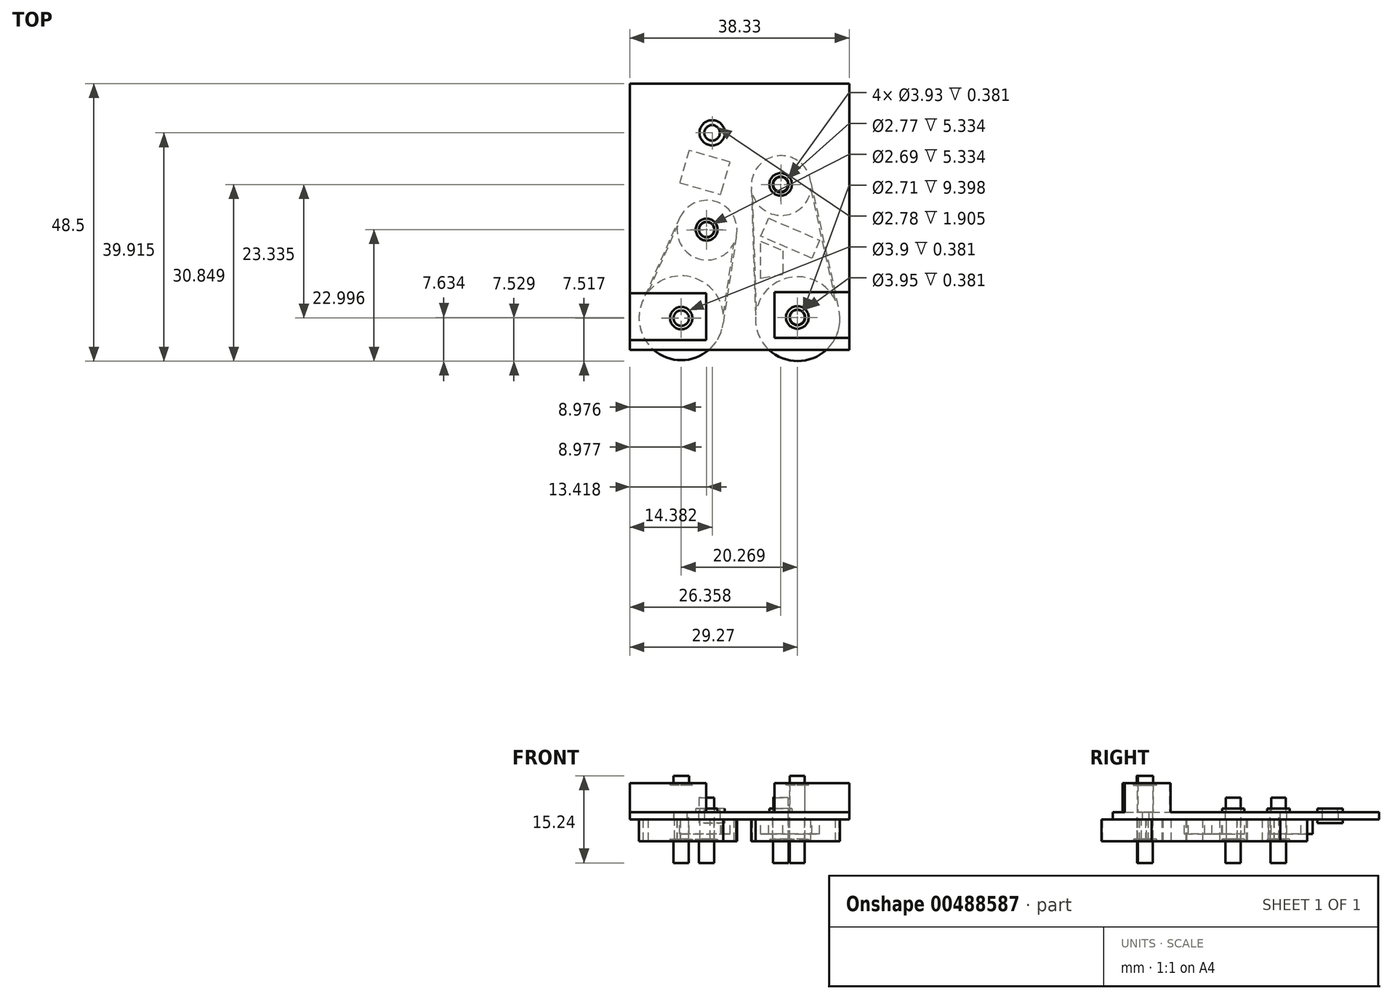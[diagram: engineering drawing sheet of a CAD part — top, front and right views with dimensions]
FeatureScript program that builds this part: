
annotation { "Feature Type Name" : "Feature", "Feature Type Description" : "" }
export const myFeature = defineFeature(function(context is Context, id is Id, definition is map)
    precondition{}
    {
        {
            var Q0;
            Q0=qCreatedBy(makeId("Top.planeOp"),FACE);
            var sketch = newSketch(context, id + "F0", { "sketchPlane" : qUnion([Q0])});
            skLineSegment(sketch, "E0", {"start": v(0, 0) * mm, "end": v(38.33, 0) * mm});
            skLineSegment(sketch, "E1", {"start": v(38.33, 0) * mm, "end": v(38.33, -46.53) * mm});
            skLineSegment(sketch, "E2", {"start": v(38.33, -46.53) * mm, "end": v(0, -46.53) * mm});
            skLineSegment(sketch, "E3", {"start": v(0, -46.53) * mm, "end": v(0, 0) * mm});
            skSolve(sketch);
        }
        {
            var Q0;
            Q0 = qSketchRegion(id + "F0", true);
            extrude(context, id + "F1", {"entities" : qUnion([Q0]), "depth" : 1.27 * mm});
        }
        {
            var Q0;
            Q0=makeQuery(id+"F1.opExtrude","CAP_FACE",FACE,{"disambiguationData":[OSD([sQuery(id+"F0.wireOp",EDGE,"E0"),sQuery(id+"F0.wireOp",EDGE,"E1"),sQuery(id+"F0.wireOp",EDGE,"E2"),sQuery(id+"F0.wireOp",EDGE,"E3")])],"isStart":true});
            var sketch = newSketch(context, id + "F2", { "sketchPlane" : qUnion([Q0])});
            skCircle(sketch, "E4", {"center": v(8.98, 40.97) * mm, "radius": 7.37 * mm});
            skCircle(sketch, "E5", {"center": v(29.32, 41.13) * mm, "radius": 7.37 * mm});
            skSolve(sketch);
        }
        {
            var Q0;
            Q0 = qSketchRegion(id + "F2", true);
            extrude(context, id + "F3", {"entities" : qUnion([Q0]), "operationType" : NewBodyOperationType.ADD, "depth" : 3.8 * mm});
        }
        {
            var Q0;
            Q0=makeQuery(id+"F1.opExtrude","CAP_FACE",FACE,{"disambiguationData":[OSD([sQuery(id+"F0.wireOp",EDGE,"E0"),sQuery(id+"F0.wireOp",EDGE,"E1"),sQuery(id+"F0.wireOp",EDGE,"E2"),sQuery(id+"F0.wireOp",EDGE,"E3")])],"isStart":true});
            var sketch = newSketch(context, id + "F4", { "sketchPlane" : qUnion([Q0])});
            skCircle(sketch, "E6", {"center": v(13.5, 25.6) * mm, "radius": 5.22 * mm});
            skCircle(sketch, "E7", {"center": v(26.44, 17.81) * mm, "radius": 5.22 * mm});
            skSolve(sketch);
        }
        {
            var Q0;
            Q0 = qSketchRegion(id + "F4", true);
            extrude(context, id + "F5", {"entities" : qUnion([Q0]), "operationType" : NewBodyOperationType.ADD, "depth" : 3.8 * mm});
        }
        {
            var Q0;
            Q0=makeQuery(id+"F1.opExtrude","CAP_FACE",FACE,{"disambiguationData":[OSD([sQuery(id+"F0.wireOp",EDGE,"E0"),sQuery(id+"F0.wireOp",EDGE,"E1"),sQuery(id+"F0.wireOp",EDGE,"E2"),sQuery(id+"F0.wireOp",EDGE,"E3")])],"isStart":true});
            var sketch = newSketch(context, id + "F6", { "sketchPlane" : qUnion([Q0])});
            skCircle(sketch, "E8", {"center": v(14.38, 8.59) * mm, "radius": 1.36 * mm});
            skSolve(sketch);
        }
        {
            var Q0;
            Q0 = qSketchRegion(id + "F6", true);
            extrude(context, id + "F7", {"entities" : qUnion([Q0]), "operationType" : NewBodyOperationType.REMOVE, "oppositeDirection" : true, "depth" : 25.4 * mm});
        }
        {
            var Q0;
            Q0=makeQuery(id+"F1.opExtrude","CAP_FACE",FACE,{"disambiguationData":[OSD([sQuery(id+"F0.wireOp",EDGE,"E0"),sQuery(id+"F0.wireOp",EDGE,"E1"),sQuery(id+"F0.wireOp",EDGE,"E2"),sQuery(id+"F0.wireOp",EDGE,"E3")])],"isStart":true});
            var sketch = newSketch(context, id + "F8", { "sketchPlane" : qUnion([Q0])});
            skCircle(sketch, "E9", {"center": v(14.38, 8.59) * mm, "radius": 2.25 * mm});
            skSolve(sketch);
        }
        {
            var Q0;
            Q0 = qSketchRegion(id + "F8", true);
            extrude(context, id + "F9", {"entities" : qUnion([Q0]), "operationType" : NewBodyOperationType.ADD, "depth" : 0.64 * mm});
        }
        {
            var Q0;
            Q0=makeQuery(id+"F9.opExtrude","CAP_FACE",FACE,{"disambiguationData":[OSD([sQuery(id+"F8.wireOp",EDGE,"E9")])],"isStart":false});
            var sketch = newSketch(context, id + "F10", { "sketchPlane" : qUnion([Q0])});
            skCircle(sketch, "E10", {"center": v(14.38, 8.59) * mm, "radius": 1.39 * mm});
            skSolve(sketch);
        }
        {
            var Q0;
            Q0 = qSketchRegion(id + "F10", true);
            extrude(context, id + "F11", {"entities" : qUnion([Q0]), "operationType" : NewBodyOperationType.REMOVE, "oppositeDirection" : true, "depth" : 25.4 * mm});
        }
        {
            var Q0;
            Q0=makeQuery(id+"F1.opExtrude","CAP_FACE",FACE,{"disambiguationData":[OSD([sQuery(id+"F0.wireOp",EDGE,"E0"),sQuery(id+"F0.wireOp",EDGE,"E1"),sQuery(id+"F0.wireOp",EDGE,"E2"),sQuery(id+"F0.wireOp",EDGE,"E3")])],"isStart":true});
            var sketch = newSketch(context, id + "F12", { "sketchPlane" : qUnion([Q0])});
            skLineSegment(sketch, "E11", {"start": v(24.24, 23.52) * mm, "end": v(33.15, 27.36) * mm});
            skLineSegment(sketch, "E12", {"start": v(33.15, 27.36) * mm, "end": v(31.8, 30.5) * mm});
            skLineSegment(sketch, "E13", {"start": v(31.8, 30.5) * mm, "end": v(22.88, 26.67) * mm});
            skLineSegment(sketch, "E14", {"start": v(22.88, 26.67) * mm, "end": v(24.24, 23.52) * mm});
            skLineSegment(sketch, "E15", {"start": v(22.88, 34.06) * mm, "end": v(22.88, 27.52) * mm});
            skLineSegment(sketch, "E16", {"start": v(22.88, 27.52) * mm, "end": v(26.75, 29.2) * mm});
            skLineSegment(sketch, "E17", {"start": v(26.75, 29.2) * mm, "end": v(26.75, 33.38) * mm});
            skLineSegment(sketch, "E18", {"start": v(26.75, 33.38) * mm, "end": v(22.88, 34.06) * mm});
            skLineSegment(sketch, "E19", {"start": v(16.03, 18.85) * mm, "end": v(17.5, 13.68) * mm});
            skLineSegment(sketch, "E20", {"start": v(17.5, 13.68) * mm, "end": v(10.33, 11.65) * mm});
            skLineSegment(sketch, "E21", {"start": v(10.33, 11.65) * mm, "end": v(8.72, 17.32) * mm});
            skLineSegment(sketch, "E22", {"start": v(8.72, 17.32) * mm, "end": v(15.86, 19.35) * mm});
            skLineSegment(sketch, "E23", {"start": v(15.86, 19.35) * mm, "end": v(16.03, 18.85) * mm});
            skSolve(sketch);
        }
        {
            var Q0;
            Q0 = qSketchRegion(id + "F12", true);
            extrude(context, id + "F13", {"entities" : qUnion([Q0]), "operationType" : NewBodyOperationType.ADD, "depth" : 2.54 * mm});
        }
        {
            var Q0;
            Q0=makeQuery(id+"F3.opExtrude","CAP_FACE",FACE,{"disambiguationData":[OSD([sQuery(id+"F2.wireOp",EDGE,"E4")])],"isStart":false});
            var sketch = newSketch(context, id + "F14", { "sketchPlane" : qUnion([Q0])});
            skCircle(sketch, "E24", {"center": v(8.98, 40.97) * mm, "radius": 1.32 * mm});
            skCircle(sketch, "E25", {"center": v(29.26, 40.85) * mm, "radius": 1.32 * mm});
            skCircle(sketch, "E26", {"center": v(13.42, 25.5) * mm, "radius": 1.32 * mm});
            skCircle(sketch, "E27", {"center": v(26.35, 17.6) * mm, "radius": 1.38 * mm});
            skSolve(sketch);
        }
        {
            var Q0;
            Q0 = qSketchRegion(id + "F14", true);
            extrude(context, id + "F15", {"entities" : qUnion([Q0]), "operationType" : NewBodyOperationType.REMOVE, "oppositeDirection" : true, "depth" : 25.4 * mm});
        }
        {
            var Q0;
            Q0=makeQuery(id+"F3.opExtrude","CAP_FACE",FACE,{"disambiguationData":[OSD([sQuery(id+"F2.wireOp",EDGE,"E4")])],"isStart":false});
            var sketch = newSketch(context, id + "F16", { "sketchPlane" : qUnion([Q0])});
            skCircle(sketch, "E28", {"center": v(8.98, 40.97) * mm, "radius": 1.96 * mm});
            skCircle(sketch, "E29", {"center": v(29.25, 40.9) * mm, "radius": 1.96 * mm});
            skCircle(sketch, "E30", {"center": v(13.37, 25.56) * mm, "radius": 1.96 * mm});
            skCircle(sketch, "E31", {"center": v(26.38, 17.64) * mm, "radius": 1.96 * mm});
            skSolve(sketch);
        }
        {
            var Q0;
            Q0 = qSketchRegion(id + "F16", true);
            extrude(context, id + "F17", {"entities" : qUnion([Q0]), "operationType" : NewBodyOperationType.REMOVE, "oppositeDirection" : true, "depth" : 0.38 * mm});
        }
        {
            var Q0;
            Q0=makeQuery(id+"F1.opExtrude","CAP_FACE",FACE,{"disambiguationData":[OSD([sQuery(id+"F0.wireOp",EDGE,"E0"),sQuery(id+"F0.wireOp",EDGE,"E1"),sQuery(id+"F0.wireOp",EDGE,"E2"),sQuery(id+"F0.wireOp",EDGE,"E3")])],"isStart":false});
            var sketch = newSketch(context, id + "F18", { "sketchPlane" : qUnion([Q0])});
            skLineSegment(sketch, "E32.bottom", {"start": v(13.33, -44.85) * mm, "end": v(0, -44.85) * mm});
            skLineSegment(sketch, "E32.top", {"start": v(13.33, -36.63) * mm, "end": v(0, -36.63) * mm});
            skLineSegment(sketch, "E32.left", {"start": v(13.33, -44.85) * mm, "end": v(13.33, -36.63) * mm});
            skLineSegment(sketch, "E32.right", {"start": v(0, -44.85) * mm, "end": v(0, -36.63) * mm});
            skLineSegment(sketch, "E33.bottom", {"start": v(25.27, -44.47) * mm, "end": v(38.33, -44.47) * mm});
            skLineSegment(sketch, "E33.top", {"start": v(25.27, -36.43) * mm, "end": v(38.33, -36.43) * mm});
            skLineSegment(sketch, "E33.left", {"start": v(25.27, -44.47) * mm, "end": v(25.27, -36.43) * mm});
            skLineSegment(sketch, "E33.right", {"start": v(38.33, -44.47) * mm, "end": v(38.33, -36.43) * mm});
            skSolve(sketch);
        }
        {
            var Q0;
            Q0 = qSketchRegion(id + "F18", true);
            extrude(context, id + "F19", {"entities" : qUnion([Q0]), "operationType" : NewBodyOperationType.ADD, "depth" : 5.08 * mm});
        }
        {
            var Q0;
            Q0=makeQuery(id+"F19.opExtrude","CAP_FACE",FACE,{"disambiguationData":[OSD([sQuery(id+"F18.wireOp",EDGE,"E33.bottom"),sQuery(id+"F18.wireOp",EDGE,"E33.top"),sQuery(id+"F18.wireOp",EDGE,"E33.left"),sQuery(id+"F18.wireOp",EDGE,"E33.right")])],"isStart":false});
            var sketch = newSketch(context, id + "F20", { "sketchPlane" : qUnion([Q0])});
            skCircle(sketch, "E34", {"center": v(29.27, -40.87) * mm, "radius": 1.35 * mm});
            skCircle(sketch, "E35", {"center": v(8.98, -40.98) * mm, "radius": 1.32 * mm});
            skSolve(sketch);
        }
        {
            var Q0;
            Q0 = qSketchRegion(id + "F20", true);
            extrude(context, id + "F21", {"entities" : qUnion([Q0]), "operationType" : NewBodyOperationType.REMOVE, "oppositeDirection" : true, "depth" : 25.4 * mm});
        }
        {
            var Q0;
            Q0=makeQuery(id+"F19.opExtrude","CAP_FACE",FACE,{"disambiguationData":[OSD([sQuery(id+"F18.wireOp",EDGE,"E33.bottom"),sQuery(id+"F18.wireOp",EDGE,"E33.top"),sQuery(id+"F18.wireOp",EDGE,"E33.left"),sQuery(id+"F18.wireOp",EDGE,"E33.right")])],"isStart":false});
            var sketch = newSketch(context, id + "F22", { "sketchPlane" : qUnion([Q0])});
            skCircle(sketch, "E36", {"center": v(29.27, -40.87) * mm, "radius": 1.98 * mm});
            skCircle(sketch, "E37", {"center": v(8.98, -40.98) * mm, "radius": 1.95 * mm});
            skSolve(sketch);
        }
        {
            var Q0;
            Q0 = qSketchRegion(id + "F22", true);
            extrude(context, id + "F23", {"entities" : qUnion([Q0]), "operationType" : NewBodyOperationType.REMOVE, "oppositeDirection" : true, "depth" : 0.38 * mm});
        }
        {
            var Q0;
            Q0=makeQuery(id+"F1.opExtrude","CAP_FACE",FACE,{"disambiguationData":[OSD([sQuery(id+"F0.wireOp",EDGE,"E0"),sQuery(id+"F0.wireOp",EDGE,"E1"),sQuery(id+"F0.wireOp",EDGE,"E2"),sQuery(id+"F0.wireOp",EDGE,"E3")])],"isStart":false});
            var sketch = newSketch(context, id + "F24", { "sketchPlane" : qUnion([Q0])});
            skCircle(sketch, "E38", {"center": v(13.42, -25.5) * mm, "radius": 1.91 * mm});
            skCircle(sketch, "E39", {"center": v(26.35, -17.6) * mm, "radius": 1.97 * mm});
            skCircle(sketch, "E40", {"center": v(14.38, -8.59) * mm, "radius": 2.2 * mm});
            skSolve(sketch);
        }
        {
            var Q0;
            Q0 = qSketchRegion(id + "F24", true);
            extrude(context, id + "F25", {"entities" : qUnion([Q0]), "operationType" : NewBodyOperationType.ADD, "depth" : 0.64 * mm});
        }
        {
            var Q0;
            Q0=makeQuery(id+"F25.opExtrude","CAP_FACE",FACE,{"disambiguationData":[OSD([sQuery(id+"F24.wireOp",EDGE,"E38")])],"isStart":false});
            var sketch = newSketch(context, id + "F26", { "sketchPlane" : qUnion([Q0])});
            skCircle(sketch, "E41", {"center": v(13.42, -25.5) * mm, "radius": 1.35 * mm});
            skCircle(sketch, "E42", {"center": v(26.36, -17.65) * mm, "radius": 1.38 * mm});
            skCircle(sketch, "E43", {"center": v(14.37, -8.6) * mm, "radius": 1.35 * mm});
            skSolve(sketch);
        }
        {
            var Q0;
            Q0 = qSketchRegion(id + "F26", true);
            extrude(context, id + "F27", {"entities" : qUnion([Q0]), "operationType" : NewBodyOperationType.REMOVE, "oppositeDirection" : true, "depth" : 25.4 * mm});
        }
        {
            var Q0;
            Q0=makeQuery(id+"F1.opExtrude","CAP_FACE",FACE,{"disambiguationData":[OSD([sQuery(id+"F0.wireOp",EDGE,"E0"),sQuery(id+"F0.wireOp",EDGE,"E1"),sQuery(id+"F0.wireOp",EDGE,"E2"),sQuery(id+"F0.wireOp",EDGE,"E3")])],"isStart":false});
            var sketch = newSketch(context, id + "F28", { "sketchPlane" : qUnion([Q0])});
            skCircle(sketch, "E44", {"center": v(29.26, -40.85) * mm, "radius": 1.3 * mm});
            skCircle(sketch, "E45", {"center": v(8.97, -41) * mm, "radius": 1.35 * mm});
            skSolve(sketch);
        }
        {
            var Q0;
            Q0 = qSketchRegion(id + "F28", true);
            extrude(context, id + "F29", {"entities" : qUnion([Q0]), "operationType" : NewBodyOperationType.ADD, "depth" : 6.35 * mm});
        }
        {
            var Q0;
            Q0=makeQuery(id+"F1.opExtrude","CAP_FACE",FACE,{"disambiguationData":[OSD([sQuery(id+"F0.wireOp",EDGE,"E0"),sQuery(id+"F0.wireOp",EDGE,"E1"),sQuery(id+"F0.wireOp",EDGE,"E2"),sQuery(id+"F0.wireOp",EDGE,"E3")])],"isStart":false});
            var sketch = newSketch(context, id + "F30", { "sketchPlane" : qUnion([Q0])});
            skCircle(sketch, "E46", {"center": v(26.35, -17.6) * mm, "radius": 1.3 * mm});
            skCircle(sketch, "E47", {"center": v(13.42, -25.5) * mm, "radius": 1.32 * mm});
            skSolve(sketch);
        }
        {
            var Q0;
            Q0 = qSketchRegion(id + "F30", true);
            extrude(context, id + "F31", {"entities" : qUnion([Q0]), "depth" : 2.54 * mm});
        }
        {
            var Q0;
            Q0=makeQuery(id+"F6.imprint","IMPRINT",FACE,{"disambiguationData":[TD([[makeQuery(id+"F6.imprint","IMPRINT",EDGE,{"derivedFrom":sQuery(id+"F6.wireOp",EDGE,"E8")}),-1.0]])]});
            var sketch = newSketch(context, id + "F32", { "sketchPlane" : qUnion([Q0])});
            skCircle(sketch, "E48", {"center": v(8.97, 40.95) * mm, "radius": 1.32 * mm});
            skCircle(sketch, "E49", {"center": v(29.26, 40.89) * mm, "radius": 1.3 * mm});
            skCircle(sketch, "E50", {"center": v(13.4, 25.52) * mm, "radius": 1.34 * mm});
            skCircle(sketch, "E51", {"center": v(26.38, 17.63) * mm, "radius": 1.36 * mm});
            skSolve(sketch);
        }
        {
            var Q0;
            Q0 = qSketchRegion(id + "F32", true);
            extrude(context, id + "F33", {"entities" : qUnion([Q0]), "operationType" : NewBodyOperationType.ADD, "depth" : 7.62 * mm});
        }
        {
            var Q0;
            Q0=makeQuery(id+"F6.imprint","IMPRINT",FACE,{"disambiguationData":[TD([[makeQuery(id+"F6.imprint","IMPRINT",EDGE,{"derivedFrom":sQuery(id+"F6.wireOp",EDGE,"E8")}),-1.0]])]});
            var sketch = newSketch(context, id + "F34", { "sketchPlane" : qUnion([Q0])});
            skLineSegment(sketch, "E52", {"start": v(8.8, 23.17) * mm, "end": v(2.16, 38.16) * mm});
            skLineSegment(sketch, "E53", {"start": v(2.16, 38.16) * mm, "end": v(2.39, 38.26) * mm});
            skLineSegment(sketch, "E54", {"start": v(2.39, 38.26) * mm, "end": v(9.07, 23.17) * mm});
            skLineSegment(sketch, "E55", {"start": v(9.07, 23.17) * mm, "end": v(8.8, 23.17) * mm});
            skSolve(sketch);
        }
        {
            var Q0;
            Q0 = qSketchRegion(id + "F34", true);
            extrude(context, id + "F35", {"entities" : qUnion([Q0]), "operationType" : NewBodyOperationType.ADD, "depth" : 3.8 * mm});
        }
        {
            var Q0;
            Q0=makeQuery(id+"F6.imprint","IMPRINT",FACE,{"disambiguationData":[TD([[makeQuery(id+"F6.imprint","IMPRINT",EDGE,{"derivedFrom":sQuery(id+"F6.wireOp",EDGE,"E8")}),-1.0]])]});
            var sketch = newSketch(context, id + "F36", { "sketchPlane" : qUnion([Q0])});
            skLineSegment(sketch, "E56", {"start": v(18.65, 26.4) * mm, "end": v(16.24, 42.2) * mm});
            skLineSegment(sketch, "E57", {"start": v(16.24, 42.2) * mm, "end": v(16.04, 42.17) * mm});
            skLineSegment(sketch, "E58", {"start": v(16.04, 42.17) * mm, "end": v(18.44, 26.4) * mm});
            skLineSegment(sketch, "E59", {"start": v(18.44, 26.4) * mm, "end": v(18.65, 26.4) * mm});
            skSolve(sketch);
        }
        {
            var Q0;
            Q0 = qSketchRegion(id + "F36", true);
            extrude(context, id + "F37", {"entities" : qUnion([Q0]), "operationType" : NewBodyOperationType.ADD, "depth" : 3.8 * mm});
        }
        {
            var Q0;
            Q0=makeQuery(id+"F6.imprint","IMPRINT",FACE,{"disambiguationData":[TD([[makeQuery(id+"F6.imprint","IMPRINT",EDGE,{"derivedFrom":sQuery(id+"F6.wireOp",EDGE,"E8")}),-1.0]])]});
            var sketch = newSketch(context, id + "F38", { "sketchPlane" : qUnion([Q0])});
            skLineSegment(sketch, "E60", {"start": v(21.23, 18.35) * mm, "end": v(21.98, 41.48) * mm});
            skLineSegment(sketch, "E61", {"start": v(21.98, 41.48) * mm, "end": v(22.18, 41.47) * mm});
            skLineSegment(sketch, "E62", {"start": v(22.18, 41.47) * mm, "end": v(21.43, 18.35) * mm});
            skLineSegment(sketch, "E63", {"start": v(21.43, 18.35) * mm, "end": v(21.23, 18.35) * mm});
            skSolve(sketch);
        }
        {
            var Q0;
            Q0 = qSketchRegion(id + "F38", true);
            extrude(context, id + "F39", {"entities" : qUnion([Q0]), "operationType" : NewBodyOperationType.ADD, "depth" : 3.8 * mm});
        }
        {
            var Q0;
            Q0=makeQuery(id+"F6.imprint","IMPRINT",FACE,{"disambiguationData":[TD([[makeQuery(id+"F6.imprint","IMPRINT",EDGE,{"derivedFrom":sQuery(id+"F6.wireOp",EDGE,"E8")}),-1.0]])]});
            var sketch = newSketch(context, id + "F40", { "sketchPlane" : qUnion([Q0])});
            skLineSegment(sketch, "E64", {"start": v(31.62, 17.21) * mm, "end": v(36.58, 39.75) * mm});
            skLineSegment(sketch, "E65", {"start": v(36.58, 39.75) * mm, "end": v(36.38, 39.8) * mm});
            skLineSegment(sketch, "E66", {"start": v(36.38, 39.8) * mm, "end": v(31.41, 17.26) * mm});
            skLineSegment(sketch, "E67", {"start": v(31.41, 17.26) * mm, "end": v(31.62, 17.21) * mm});
            skSolve(sketch);
        }
        {
            var Q0;
            Q0 = qSketchRegion(id + "F40", true);
            extrude(context, id + "F41", {"entities" : qUnion([Q0]), "operationType" : NewBodyOperationType.ADD, "depth" : 3.8 * mm});
        }
    });
